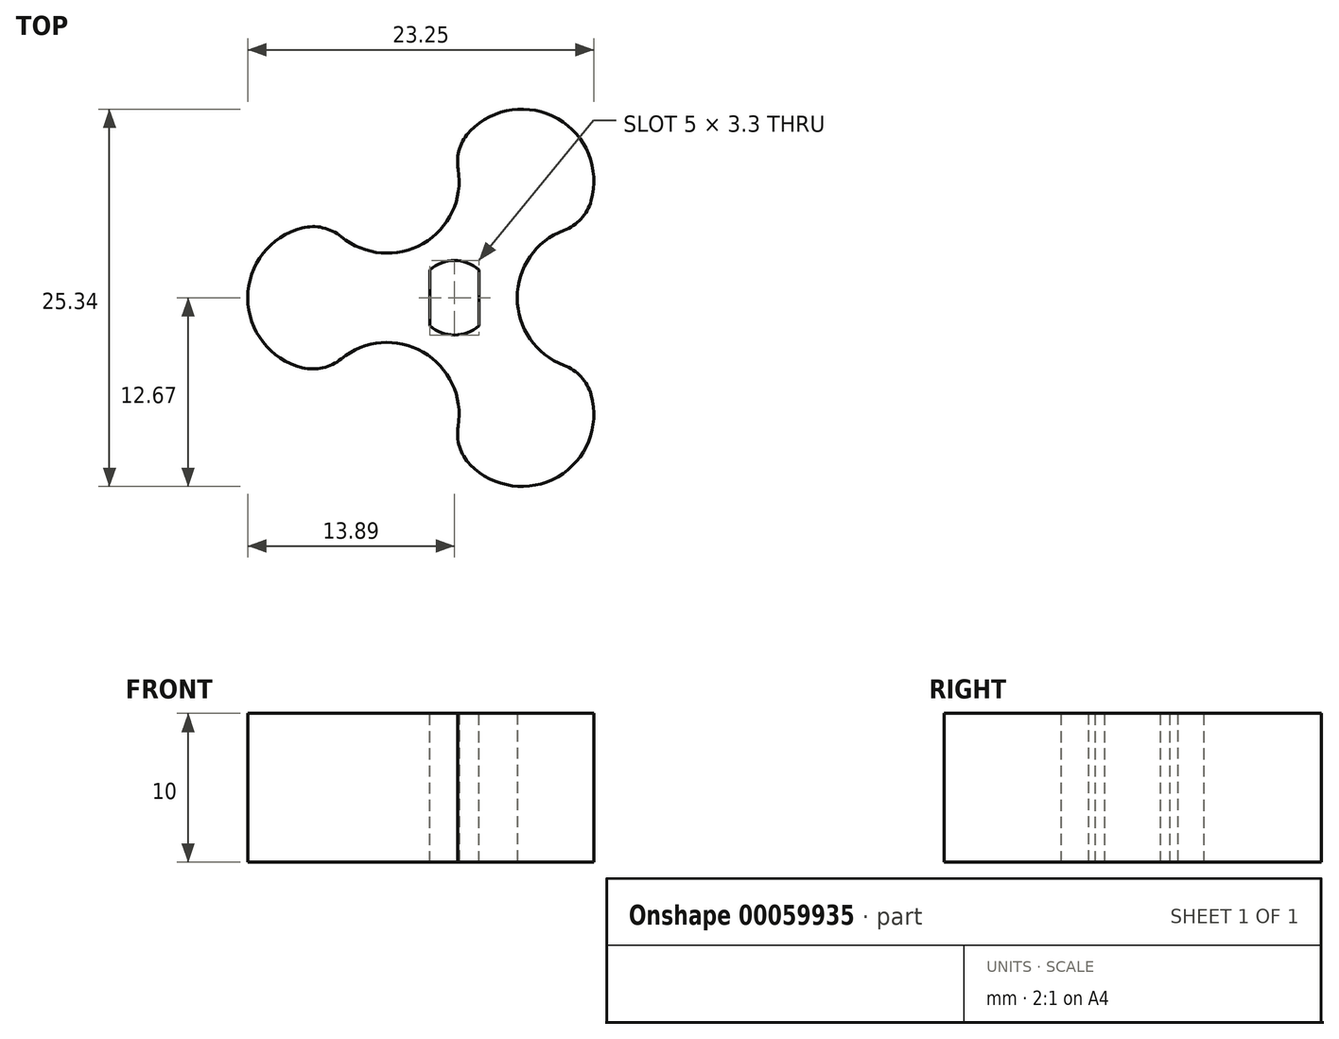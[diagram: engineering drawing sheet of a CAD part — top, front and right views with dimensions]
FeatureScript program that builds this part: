
annotation { "Feature Type Name" : "Feature", "Feature Type Description" : "" }
export const myFeature = defineFeature(function(context is Context, id is Id, definition is map)
    precondition{}
    {
        {
            var Q0;
            Q0=qCreatedBy(makeId("Top.planeOp"),FACE);
            var sketch = newSketch(context, id + "F0", { "sketchPlane" : qUnion([Q0])});
            skLineSegment(sketch, "E0", {"start": v(0, 0) * mm, "end": v(0, 9.55) * mm});
            skLineSegment(sketch, "E1", {"start": v(0, 0) * mm, "end": v(8.27, -4.77) * mm, "construction": true});
            skArc(sketch, "E2", {"start": v(8.27, 4.77) * mm, "mid": v(6.94, 12.03) * mm, "end": v(0, 9.55) * mm});
            skArc(sketch, "E3", {"start": v(8.27, 4.77) * mm, "mid": v(4.21, 0) * mm, "end": v(8.27, -4.77) * mm});
            skCircle(sketch, "E4", {"center": v(0, 0) * mm, "radius": 9.55 * mm, "construction": true});
            skLineSegment(sketch, "E5", {"start": v(0, 0) * mm, "end": v(8.27, 4.77) * mm, "construction": true});
            skCircle(sketch, "E6", {"center": v(0, 0) * mm, "radius": 9.05 * mm, "construction": true});
            skCircle(sketch, "E7", {"center": v(0, 0) * mm, "radius": 10.05 * mm, "construction": true});
            skLineSegment(sketch, "E8", {"start": v(0, 9.05) * mm, "end": v(0, 9.55) * mm});
            skLineSegment(sketch, "E9", {"start": v(0, 9.55) * mm, "end": v(0, 10.05) * mm});
            skArc(sketch, "E10.1.0", {"start": v(-8.27, 4.77) * mm, "mid": v(-2.1, 3.65) * mm, "end": v(0, 9.55) * mm});
            skArc(sketch, "E10.1.1", {"start": v(-8.27, 4.77) * mm, "mid": v(-13.89, 0) * mm, "end": v(-8.27, -4.77) * mm});
            skArc(sketch, "E10.2.0", {"start": v(0, -9.55) * mm, "mid": v(-2.1, -3.65) * mm, "end": v(-8.27, -4.77) * mm});
            skArc(sketch, "E10.2.1", {"start": v(0, -9.55) * mm, "mid": v(6.94, -12.03) * mm, "end": v(8.27, -4.77) * mm});
            skSolve(sketch);
        }
        {
            var Q0;
            {var subQ4=sQuery(id+"F0.wireOp",EDGE,"E2");Q0=makeQuery(id+"F0.imprint","IMPRINT",FACE,{"disambiguationData":[TD([[makeQuery(id+"F0.imprint","IMPRINT",EDGE,{"derivedFrom":subQ4}),1.0]])]});}
            extrude(context, id + "F1", {"entities" : qUnion([Q0]), "depth" : 10 * mm});
        }
        {
            var Q0;
            Q0=makeQuery(id+"F1.opExtrude","CAP_FACE",FACE,{"disambiguationData":[OSD([sQuery(id+"F0.wireOp",EDGE,"E2"),sQuery(id+"F0.wireOp",EDGE,"E3"),sQuery(id+"F0.wireOp",EDGE,"57e98310-cc7a-4a91-9270-3eaa45b5c28b.1.0"),sQuery(id+"F0.wireOp",EDGE,"57e98310-cc7a-4a91-9270-3eaa45b5c28b.1.1"),sQuery(id+"F0.wireOp",EDGE,"57e98310-cc7a-4a91-9270-3eaa45b5c28b.2.0"),sQuery(id+"F0.wireOp",EDGE,"57e98310-cc7a-4a91-9270-3eaa45b5c28b.2.1")])],"isStart":false});
            var sketch = newSketch(context, id + "F2", { "sketchPlane" : qUnion([Q0])});
            skArc(sketch, "E11", {"start": v(-1.65, -1.88) * mm, "mid": v(0, -2.5) * mm, "end": v(1.65, -1.88) * mm});
            skLineSegment(sketch, "E12", {"start": v(-1.65, 1.88) * mm, "end": v(-1.65, -1.88) * mm});
            skLineSegment(sketch, "E13", {"start": v(0, 2.5) * mm, "end": v(0, -2.5) * mm, "construction": true});
            skLineSegment(sketch, "E14.MirrorCS", {"start": v(1.65, 1.88) * mm, "end": v(1.65, -1.88) * mm});
            skArc(sketch, "E15.trimOffspring", {"start": v(1.65, 1.88) * mm, "mid": v(0, 2.5) * mm, "end": v(-1.65, 1.88) * mm});
            skSolve(sketch);
        }
        {
            var Q0;
            Q0 = qSketchRegion(id + "F2", true);
            extrude(context, id + "F3", {"entities" : qUnion([Q0]), "operationType" : NewBodyOperationType.REMOVE, "endBound" : BoundingType.THROUGH_ALL, "oppositeDirection" : true, "depth" : 25 * mm});
        }
        {
            var Q0;
            Q0=makeQuery(id+"F1.opExtrude","SWEPT_EDGE",EDGE,{"disambiguationData":[OSD([sQuery(id+"F0.wireOp",EDGE,"E2"),sQuery(id+"F0.wireOp",EDGE,"E8"),sQuery(id+"F0.wireOp",EDGE,"E10.1.0")])]});
            var Q1;
            Q1=makeQuery(id+"F1.opExtrude","SWEPT_EDGE",EDGE,{"disambiguationData":[OSD([sQuery(id+"F0.wireOp",EDGE,"E2"),sQuery(id+"F0.wireOp",EDGE,"E3")])]});
            var Q2;
            Q2=makeQuery(id+"F1.opExtrude","SWEPT_EDGE",EDGE,{"disambiguationData":[OSD([sQuery(id+"F0.wireOp",EDGE,"E3"),sQuery(id+"F0.wireOp",EDGE,"E10.2.1")])]});
            var Q3;
            Q3=makeQuery(id+"F1.opExtrude","SWEPT_EDGE",EDGE,{"disambiguationData":[OSD([sQuery(id+"F0.wireOp",EDGE,"E10.1.1"),sQuery(id+"F0.wireOp",EDGE,"E10.2.0")])]});
            var Q4;
            Q4=makeQuery(id+"F1.opExtrude","SWEPT_EDGE",EDGE,{"disambiguationData":[OSD([sQuery(id+"F0.wireOp",EDGE,"E10.1.0"),sQuery(id+"F0.wireOp",EDGE,"E10.1.1")])]});
            var Q5;
            Q5=makeQuery(id+"F1.opExtrude","SWEPT_EDGE",EDGE,{"disambiguationData":[OSD([sQuery(id+"F0.wireOp",EDGE,"E10.2.0"),sQuery(id+"F0.wireOp",EDGE,"E10.2.1")])]});
            fillet(context, id + "F4", {"entities" : qUnion([Q0, Q1, Q2, Q3, Q4, Q5]), "radius" : 3 * mm, "tangentPropagation" : true, "allowEdgeOverflow" : false});
        }
    });
